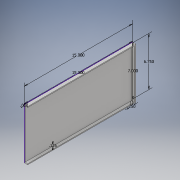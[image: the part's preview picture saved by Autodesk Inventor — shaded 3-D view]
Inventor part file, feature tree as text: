
AUTODESK INVENTOR PART (.ipt)
format: ipt  version: 2017 (Build 210142000, 142)  size: 113,152 bytes
history: native  units: in
note: dims shown in document units (in); Inventor stores cm internally (conversion verified against a paired STEP export)
features: extrude x3, sketch x1
ambient origin geometry x8: Origin, YZ Plane, XZ Plane, XY Plane, X Axis, Y Axis, Z Axis, Center Point
bodies: Solid1 (feature_tree)
feature tree (4):
  sketch  "Sketch1"  dims[d0=7.0in d1=15.0in d2=6.75in d3=15.0in d4=0.0in d5=0.125in d6=0.125in d7=0.0in d8=0.5in d9=0.0in d10=0.25in d11=0.5in d12=0.0in]
  extrude  "Extrusion1"  Depth=15.0in
  extrude  "Extrusion2"  Depth=6.75in
  extrude  "Extrusion3"  Depth=15.0in
